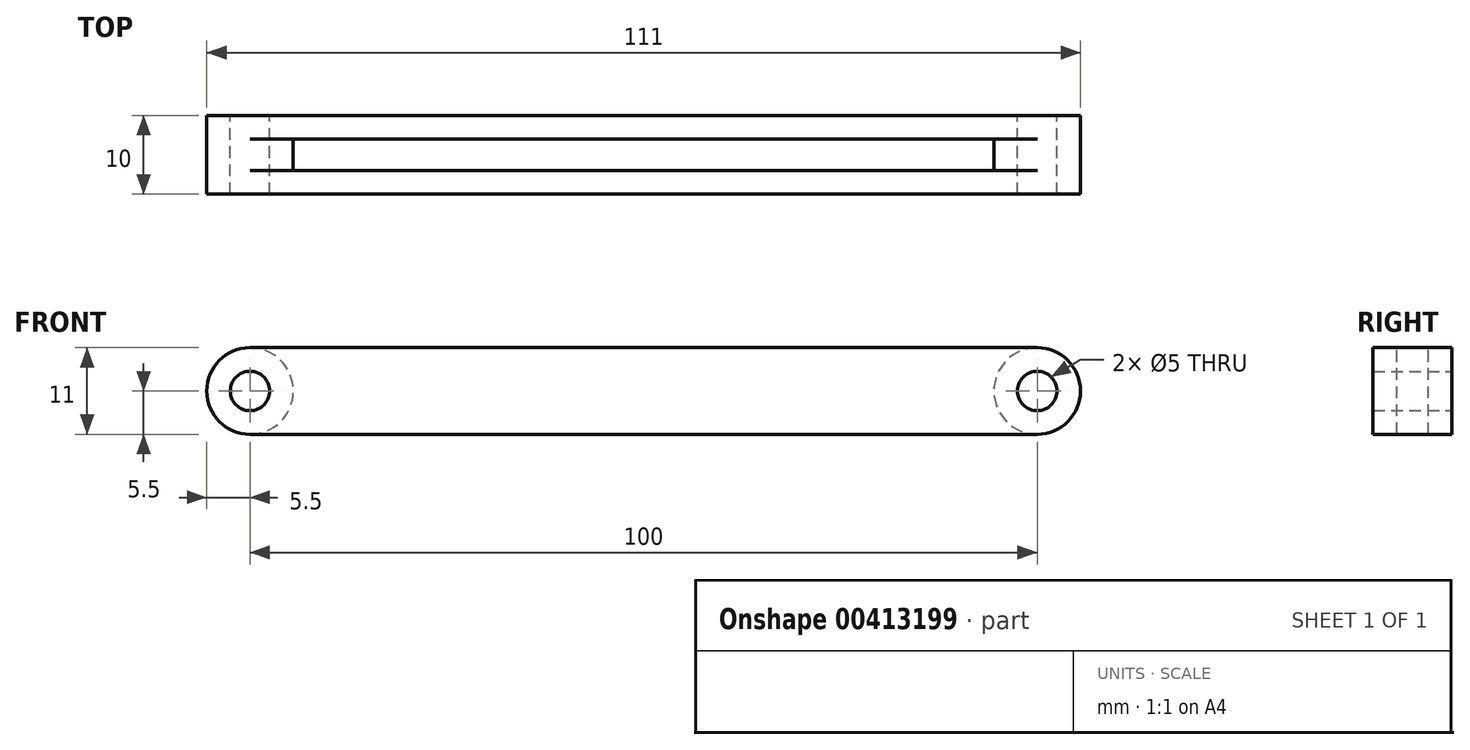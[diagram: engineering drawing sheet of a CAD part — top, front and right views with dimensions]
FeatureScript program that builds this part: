
annotation { "Feature Type Name" : "Feature", "Feature Type Description" : "" }
export const myFeature = defineFeature(function(context is Context, id is Id, definition is map)
    precondition{}
    {
        {
            var Q0;
            Q0=qCreatedBy(makeId("Front.planeOp"),FACE);
            var sketch = newSketch(context, id + "F0", { "sketchPlane" : qUnion([Q0])});
            skLineSegment(sketch, "E0", {"start": v(-106.4, 0) * mm, "end": v(105.97, 0) * mm, "construction": true});
            skLineSegment(sketch, "E1", {"start": v(0, 59.7) * mm, "end": v(0, -59.45) * mm, "construction": true});
            skPoint(sketch, "E2", {"position": v(0, 0) * mm});
            skLineSegment(sketch, "E3", {"start": v(-50, 5.5) * mm, "end": v(0, 5.5) * mm});
            skLineSegment(sketch, "E4", {"start": v(-50, -5.5) * mm, "end": v(0, -5.5) * mm});
            skLineSegment(sketch, "E5", {"start": v(-50, 5.5) * mm, "end": v(-50, 0) * mm, "construction": true});
            skLineSegment(sketch, "E6", {"start": v(-50, 0) * mm, "end": v(-50, -5.5) * mm, "construction": true});
            skLineSegment(sketch, "E7", {"start": v(50, 5.5) * mm, "end": v(50, 0) * mm, "construction": true});
            skLineSegment(sketch, "E8", {"start": v(50, 0) * mm, "end": v(50, -5.5) * mm, "construction": true});
            skLineSegment(sketch, "E9", {"start": v(0, 5.5) * mm, "end": v(50, 5.5) * mm});
            skLineSegment(sketch, "E10", {"start": v(0, -5.5) * mm, "end": v(50, -5.5) * mm});
            skArc(sketch, "E11", {"start": v(-50, 5.5) * mm, "mid": v(-55.5, 0) * mm, "end": v(-50, -5.5) * mm});
            skArc(sketch, "E12", {"start": v(50, 5.5) * mm, "mid": v(55.5, 0) * mm, "end": v(50, -5.5) * mm});
            skCircle(sketch, "E13", {"center": v(-50, 0) * mm, "radius": 2.5 * mm});
            skCircle(sketch, "E14", {"center": v(50, 0) * mm, "radius": 2.5 * mm});
            skPoint(sketch, "E15", {"position": v(-50, 2.5) * mm});
            skSolve(sketch);
        }
        {
            var Q0;
            Q0=makeQuery(id+"F0.imprint","IMPRINT",FACE,{"disambiguationData":[TD([[makeQuery(id+"F0.imprint","IMPRINT",EDGE,{"derivedFrom":sQuery(id+"F0.wireOp",EDGE,"E3")}),-1.0]])]});
            extrude(context, id + "F1", {"entities" : qUnion([Q0]), "depth" : 10 * mm});
        }
        {
            var Q0;
            Q0=makeQuery(id+"F1.opExtrude","SWEPT_FACE",FACE,{"disambiguationData":[OSD([sQuery(id+"F0.wireOp",EDGE,"E4"),sQuery(id+"F0.wireOp",EDGE,"E10")])]});
            var Q1;
            Q1=makeQuery(id+"F1.opExtrude","SWEPT_FACE",FACE,{"disambiguationData":[OSD([sQuery(id+"F0.wireOp",EDGE,"E3"),sQuery(id+"F0.wireOp",EDGE,"E9")])]});
            shell(context, id + "F2", {"entities" : qUnion([Q0, Q1]), "thickness" : 3 * mm});
        }
    });
